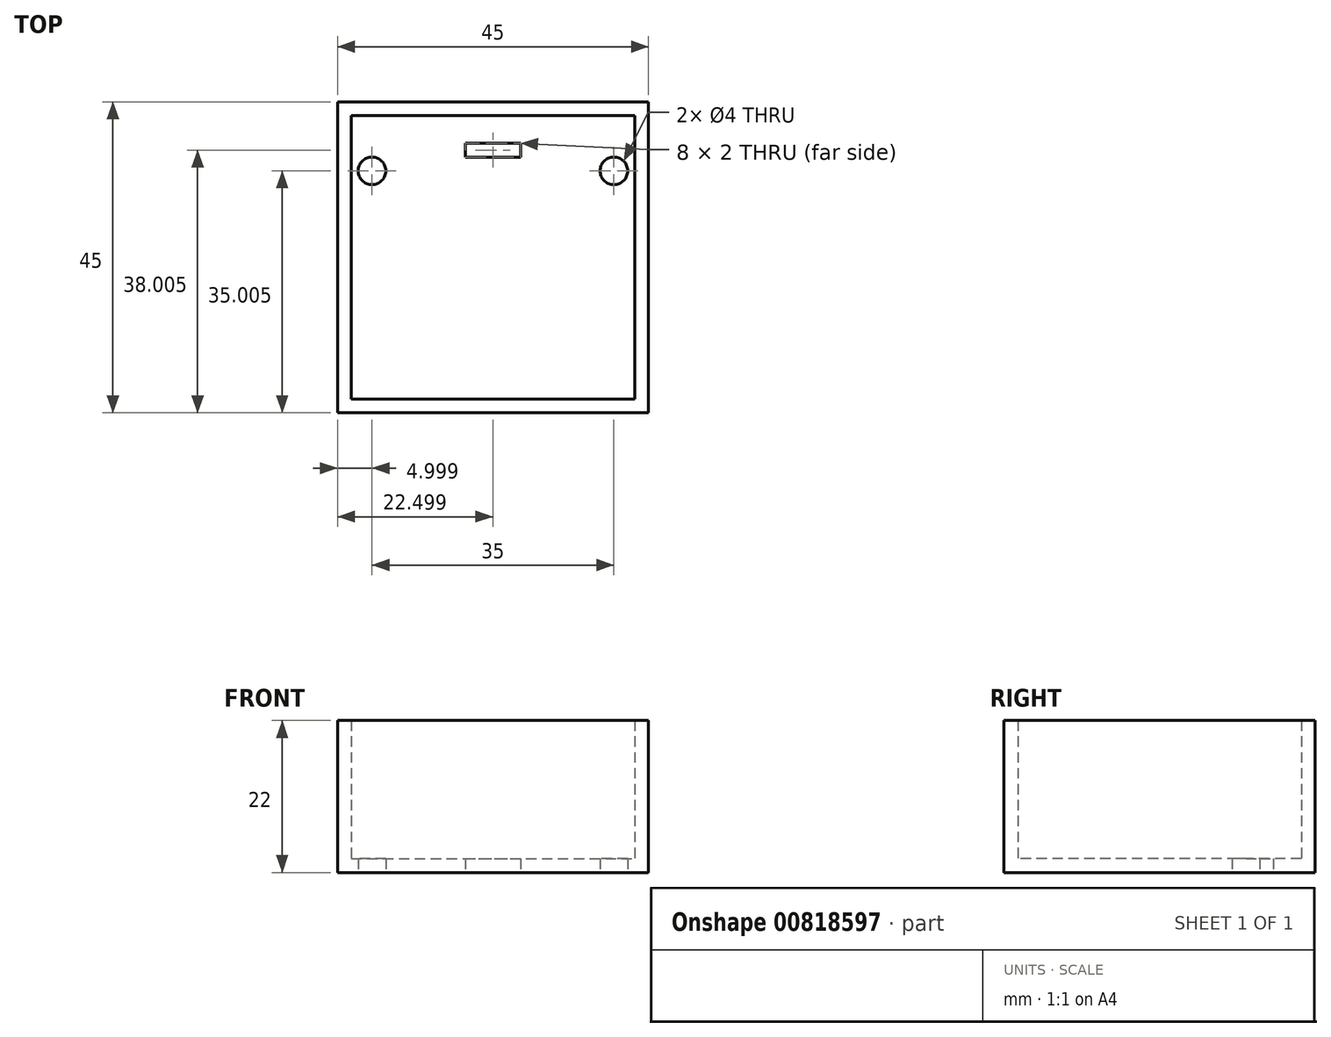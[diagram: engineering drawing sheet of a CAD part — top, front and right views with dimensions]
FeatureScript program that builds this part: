
annotation { "Feature Type Name" : "Feature", "Feature Type Description" : "" }
export const myFeature = defineFeature(function(context is Context, id is Id, definition is map)
    precondition{}
    {
        {
            var Q0;
            Q0=qCreatedBy(makeId("Top.planeOp"),FACE);
            var sketch = newSketch(context, id + "F0", { "sketchPlane" : qUnion([Q0])});
            skLineSegment(sketch, "E0.bottom", {"start": v(-65.22, 5.9) * mm, "end": v(-20.22, 5.9) * mm});
            skLineSegment(sketch, "E0.top", {"start": v(-65.22, -39.1) * mm, "end": v(-20.22, -39.1) * mm});
            skLineSegment(sketch, "E0.left", {"start": v(-65.22, 5.9) * mm, "end": v(-65.22, -39.1) * mm});
            skLineSegment(sketch, "E0.right", {"start": v(-20.22, 5.9) * mm, "end": v(-20.22, -39.1) * mm});
            skSolve(sketch);
        }
        {
            var Q0;
            Q0=makeQuery(id+"F0.imprint","IMPRINT",FACE,{"disambiguationData":[TD([[makeQuery(id+"F0.imprint","IMPRINT",EDGE,{"derivedFrom":sQuery(id+"F0.wireOp",EDGE,"E0.bottom")}),-1.0]])]});
            extrude(context, id + "F1", {"entities" : qUnion([Q0]), "depth" : 2 * mm, "offsetDistance" : 25 * mm});
        }
        {
            var Q0;
            Q0=makeQuery(id+"F1.opExtrude","CAP_FACE",FACE,{"disambiguationData":[OSD([sQuery(id+"F0.wireOp",EDGE,"E0.bottom"),sQuery(id+"F0.wireOp",EDGE,"E0.top"),sQuery(id+"F0.wireOp",EDGE,"E0.left"),sQuery(id+"F0.wireOp",EDGE,"E0.right")])],"isStart":false});
            var sketch = newSketch(context, id + "F2", { "sketchPlane" : qUnion([Q0])});
            skLineSegment(sketch, "E1.0", {"start": v(-63.22, 3.9) * mm, "end": v(-22.22, 3.9) * mm});
            skLineSegment(sketch, "E1.1", {"start": v(-63.22, 3.9) * mm, "end": v(-63.22, -37.1) * mm});
            skLineSegment(sketch, "E1.2", {"start": v(-63.22, -37.1) * mm, "end": v(-22.22, -37.1) * mm});
            skLineSegment(sketch, "E1.3", {"start": v(-22.22, 3.9) * mm, "end": v(-22.22, -37.1) * mm});
            skLineSegment(sketch, "E2.0", {"start": v(-65.22, 5.9) * mm, "end": v(-65.22, -39.1) * mm});
            skLineSegment(sketch, "E3.0", {"start": v(-65.22, 5.9) * mm, "end": v(-20.22, 5.9) * mm});
            skLineSegment(sketch, "E4.0", {"start": v(-65.22, -39.1) * mm, "end": v(-20.22, -39.1) * mm});
            skLineSegment(sketch, "E5.0", {"start": v(-20.22, 5.9) * mm, "end": v(-20.22, -39.1) * mm});
            skSolve(sketch);
        }
        {
            var Q0;
            Q0 = qSketchRegion(id + "F2", true);
            extrude(context, id + "F3", {"entities" : qUnion([Q0]), "operationType" : NewBodyOperationType.ADD, "depth" : 20 * mm, "offsetDistance" : 25 * mm});
        }
        {
            var Q0;
            Q0=makeQuery(id+"F1.opExtrude","CAP_FACE",FACE,{"disambiguationData":[OSD([sQuery(id+"F0.wireOp",EDGE,"E0.bottom"),sQuery(id+"F0.wireOp",EDGE,"E0.top"),sQuery(id+"F0.wireOp",EDGE,"E0.left"),sQuery(id+"F0.wireOp",EDGE,"E0.right")])],"isStart":true});
            var sketch = newSketch(context, id + "F4", { "sketchPlane" : qUnion([Q0])});
            skLineSegment(sketch, "E6", {"start": v(-42.72, -5.9) * mm, "end": v(-42.72, 1.1) * mm, "construction": true});
            skLineSegment(sketch, "E7.0", {"start": v(-63.72, -0.9) * mm, "end": v(-56.72, -0.9) * mm, "construction": true});
            skLineSegment(sketch, "E8", {"start": v(-56.72, -0.9) * mm, "end": v(-28.72, -0.9) * mm, "construction": true});
            skPoint(sketch, "E9", {"position": v(-42.72, -0.9) * mm});
            skLineSegment(sketch, "E10.bottom", {"start": v(-46.72, 2.1) * mm, "end": v(-38.72, 2.1) * mm});
            skLineSegment(sketch, "E10.top", {"start": v(-46.72, 0.1) * mm, "end": v(-38.72, 0.1) * mm});
            skLineSegment(sketch, "E10.left", {"start": v(-46.72, 2.1) * mm, "end": v(-46.72, 0.1) * mm});
            skLineSegment(sketch, "E10.right", {"start": v(-38.72, 2.1) * mm, "end": v(-38.72, 0.1) * mm});
            skPoint(sketch, "E10.middle", {"position": v(-42.72, 1.1) * mm});
            skSolve(sketch);
        }
        {
            var Q0;
            Q0 = qSketchRegion(id + "F4", true);
            extrude(context, id + "F5", {"entities" : qUnion([Q0]), "operationType" : NewBodyOperationType.REMOVE, "endBound" : BoundingType.UP_TO_NEXT, "oppositeDirection" : true, "depth" : 25 * mm, "offsetDistance" : 25 * mm});
        }
        {
            var Q0;
            Q0=makeQuery(id+"F1.opExtrude","CAP_FACE",FACE,{"disambiguationData":[OSD([sQuery(id+"F0.wireOp",EDGE,"E0.bottom"),sQuery(id+"F0.wireOp",EDGE,"E0.top"),sQuery(id+"F0.wireOp",EDGE,"E0.left"),sQuery(id+"F0.wireOp",EDGE,"E0.right")])],"isStart":true});
            var sketch = newSketch(context, id + "F6", { "sketchPlane" : qUnion([Q0])});
            skLineSegment(sketch, "E11.0", {"start": v(-21.72, -0.9) * mm, "end": v(-28.72, -0.9) * mm});
            skLineSegment(sketch, "E12.bottom", {"start": v(-28.72, -0.9) * mm, "end": v(-21.72, -0.9) * mm, "construction": true});
            skLineSegment(sketch, "E12.top", {"start": v(-28.72, 9.1) * mm, "end": v(-21.72, 9.1) * mm, "construction": true});
            skLineSegment(sketch, "E12.left", {"start": v(-28.72, -0.9) * mm, "end": v(-28.72, 9.1) * mm, "construction": true});
            skLineSegment(sketch, "E12.right", {"start": v(-21.72, -0.9) * mm, "end": v(-21.72, 9.1) * mm, "construction": true});
            skLineSegment(sketch, "E13.0", {"start": v(-56.72, -5.9) * mm, "end": v(-28.72, -5.9) * mm, "construction": true});
            skPoint(sketch, "E14", {"position": v(-42.72, -5.9) * mm});
            skLineSegment(sketch, "E15", {"start": v(-42.72, -5.9) * mm, "end": v(-42.72, 8.14) * mm, "construction": true});
            skLineSegment(sketch, "E16", {"start": v(-21.72, 9.1) * mm, "end": v(-28.72, -0.9) * mm, "construction": true});
            skLineSegment(sketch, "E17", {"start": v(-21.72, -0.9) * mm, "end": v(-28.72, 9.1) * mm, "construction": true});
            skPoint(sketch, "E18", {"position": v(-25.22, 4.1) * mm});
            skCircle(sketch, "E19", {"center": v(-25.22, 4.1) * mm, "radius": 2 * mm});
            skCircle(sketch, "E20.MirrorC", {"center": v(-60.22, 4.1) * mm, "radius": 2 * mm});
            skSolve(sketch);
        }
        {
            var Q0;
            Q0 = qSketchRegion(id + "F6", true);
            extrude(context, id + "F7", {"entities" : qUnion([Q0]), "operationType" : NewBodyOperationType.REMOVE, "oppositeDirection" : true, "depth" : 25 * mm, "offsetDistance" : 25 * mm});
        }
    });
